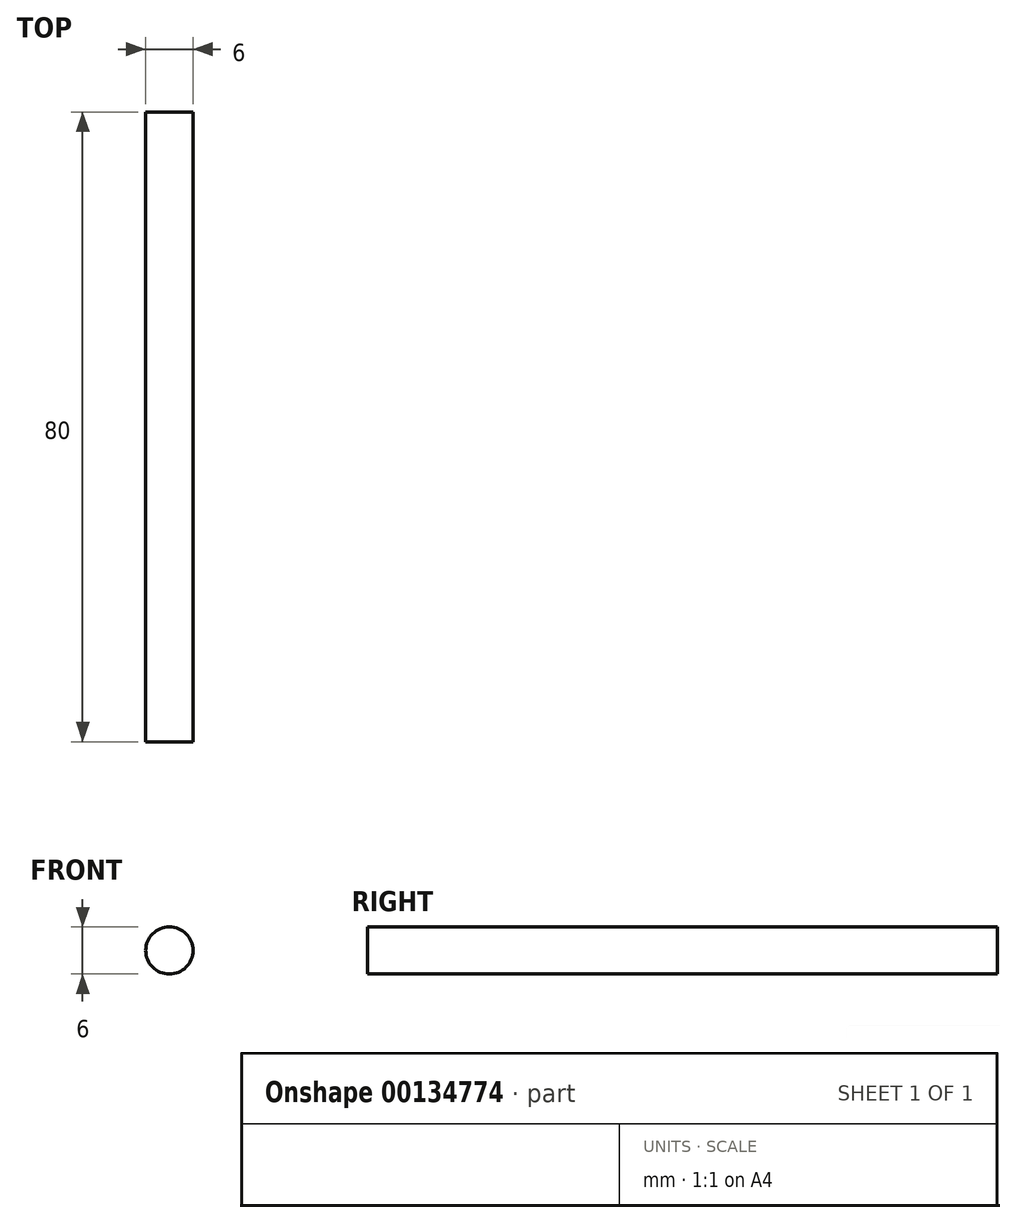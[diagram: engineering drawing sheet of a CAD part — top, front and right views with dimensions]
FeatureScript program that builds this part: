
annotation { "Feature Type Name" : "Feature", "Feature Type Description" : "" }
export const myFeature = defineFeature(function(context is Context, id is Id, definition is map)
    precondition{}
    {
        {
            var Q0;
            Q0=qCreatedBy(makeId("Front.planeOp"),FACE);
            var sketch = newSketch(context, id + "F0", { "sketchPlane" : qUnion([Q0])});
            skCircle(sketch, "E0", {"center": v(0, 0) * mm, "radius": 3 * mm});
            skSolve(sketch);
        }
        {
            var Q0;
            Q0=makeQuery(id+"F0.imprint","IMPRINT",FACE,{"disambiguationData":[TD([[makeQuery(id+"F0.imprint","IMPRINT",EDGE,{"derivedFrom":sQuery(id+"F0.wireOp",EDGE,"E0")}),1.0]])]});
            extrude(context, id + "F1", {"entities" : qUnion([Q0]), "depth" : 80 * mm});
        }
    });
